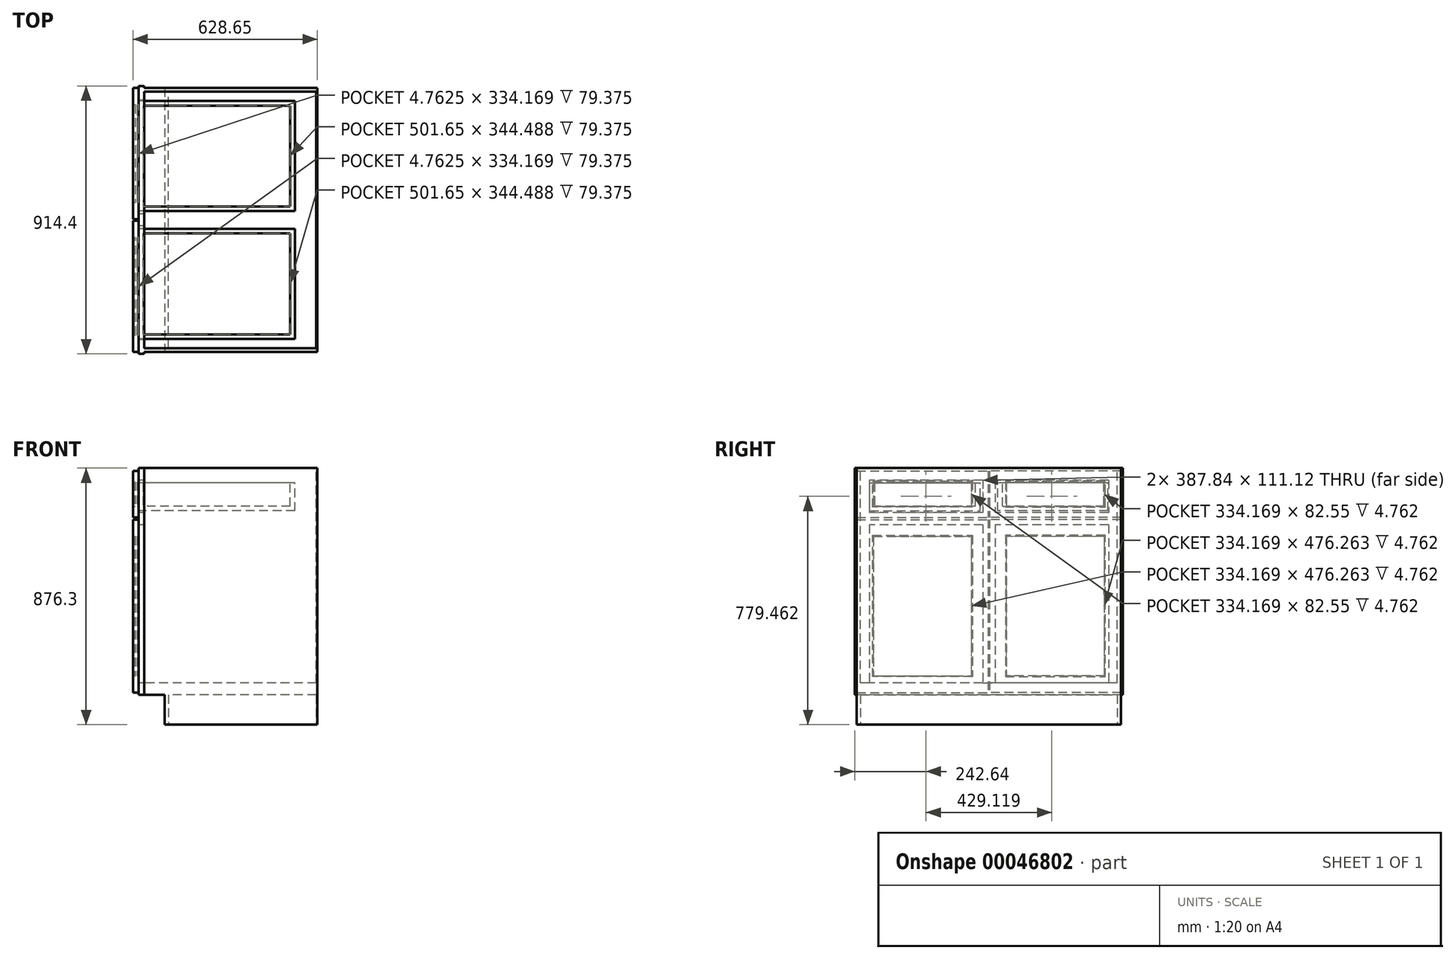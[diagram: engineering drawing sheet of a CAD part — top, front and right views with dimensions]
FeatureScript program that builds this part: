
annotation { "Feature Type Name" : "Feature", "Feature Type Description" : "" }
export const myFeature = defineFeature(function(context is Context, id is Id, definition is map)
    precondition{}
    {
        {
            var Q0;
            Q0=qCreatedBy(makeId("Front.planeOp"),FACE);
            var sketch = newSketch(context, id + "F0", { "sketchPlane" : qUnion([Q0])});
            skLineSegment(sketch, "E0.bottom", {"start": v(-304.8, -438.15) * mm, "end": v(304.8, -438.15) * mm});
            skLineSegment(sketch, "E0.top", {"start": v(-304.8, 438.15) * mm, "end": v(304.8, 438.15) * mm});
            skLineSegment(sketch, "E0.left", {"start": v(-304.8, -438.15) * mm, "end": v(-304.8, 438.15) * mm});
            skLineSegment(sketch, "E0.right", {"start": v(304.8, -438.15) * mm, "end": v(304.8, 438.15) * mm});
            skLineSegment(sketch, "E1", {"start": v(-304.8, -438.15) * mm, "end": v(304.8, 438.15) * mm, "construction": true});
            skSolve(sketch);
        }
        {
            var Q0;
            Q0=qSketchRegion(id+"F0",true);
            extrude(context, id + "F1", {"entities" : qUnion([Q0]), "oppositeDirection" : true, "depth" : 914.4 * mm});
        }
        {
            var Q0;
            Q0=makeQuery(id+"F1.opExtrude","CAP_FACE",FACE,{"disambiguationData":[OSD([sQuery(id+"F0.wireOp",EDGE,"E0.bottom"),sQuery(id+"F0.wireOp",EDGE,"E0.top"),sQuery(id+"F0.wireOp",EDGE,"E0.left"),sQuery(id+"F0.wireOp",EDGE,"E0.right")])],"isStart":true});
            var sketch = newSketch(context, id + "F2", { "sketchPlane" : qUnion([Q0])});
            skLineSegment(sketch, "E2.bottom", {"start": v(-304.8, -438.15) * mm, "end": v(-215.9, -438.15) * mm});
            skLineSegment(sketch, "E2.top", {"start": v(-304.8, -336.55) * mm, "end": v(-215.9, -336.55) * mm});
            skLineSegment(sketch, "E2.left", {"start": v(-304.8, -438.15) * mm, "end": v(-304.8, -336.55) * mm});
            skLineSegment(sketch, "E2.right", {"start": v(-215.9, -438.15) * mm, "end": v(-215.9, -336.55) * mm});
            skSolve(sketch);
        }
        {
            var Q0;
            Q0=qSketchRegion(id+"F2",true);
            extrude(context, id + "F3", {"entities" : qUnion([Q0]), "operationType" : NewBodyOperationType.REMOVE, "endBound" : BoundingType.THROUGH_ALL, "oppositeDirection" : true, "depth" : 25.4 * mm});
        }
        {
            var Q0;
            Q0=makeQuery(id+"F1.opExtrude","SWEPT_FACE",FACE,{"disambiguationData":[OSD([sQuery(id+"F0.wireOp",EDGE,"E0.left")])]});
            var sketch = newSketch(context, id + "F4", { "sketchPlane" : qUnion([Q0])});
            skLineSegment(sketch, "E3.bottom", {"start": v(-865.68, 396.88) * mm, "end": v(-48.72, 396.88) * mm});
            skLineSegment(sketch, "E3.top", {"start": v(-865.68, -295.28) * mm, "end": v(-48.72, -295.28) * mm});
            skLineSegment(sketch, "E3.left", {"start": v(-865.68, 396.88) * mm, "end": v(-865.68, -295.28) * mm});
            skLineSegment(sketch, "E3.right", {"start": v(-48.72, 396.88) * mm, "end": v(-48.72, -295.28) * mm});
            skLineSegment(sketch, "E4", {"start": v(-914.4, 438.15) * mm, "end": v(0, -336.55) * mm, "construction": true});
            skSolve(sketch);
        }
        {
            var Q0;
            Q0=qSketchRegion(id+"F4",true);
            extrude(context, id + "F5", {"entities" : qUnion([Q0]), "operationType" : NewBodyOperationType.REMOVE, "oppositeDirection" : true, "depth" : 19.05 * mm});
        }
        {
            var Q0;
            Q0=makeQuery(id+"F1.opExtrude","SWEPT_FACE",FACE,{"disambiguationData":[OSD([sQuery(id+"F0.wireOp",EDGE,"E0.top")])]});
            var sketch = newSketch(context, id + "F6", { "sketchPlane" : qUnion([Q0])});
            skLineSegment(sketch, "E5.bottom", {"start": v(304.8, 914.4) * mm, "end": v(-285.75, 914.4) * mm});
            skLineSegment(sketch, "E5.top", {"start": v(304.8, 908.05) * mm, "end": v(-285.75, 908.05) * mm});
            skLineSegment(sketch, "E5.left", {"start": v(304.8, 914.4) * mm, "end": v(304.8, 908.05) * mm});
            skLineSegment(sketch, "E5.right", {"start": v(-285.75, 914.4) * mm, "end": v(-285.75, 908.05) * mm});
            skLineSegment(sketch, "E6.bottom", {"start": v(304.8, 0) * mm, "end": v(-285.75, 0) * mm});
            skLineSegment(sketch, "E6.top", {"start": v(304.8, 6.35) * mm, "end": v(-285.75, 6.35) * mm});
            skLineSegment(sketch, "E6.left", {"start": v(304.8, 0) * mm, "end": v(304.8, 6.35) * mm});
            skLineSegment(sketch, "E6.right", {"start": v(-285.75, 0) * mm, "end": v(-285.75, 6.35) * mm});
            skSolve(sketch);
        }
        {
            var Q0;
            Q0=qSketchRegion(id+"F6",true);
            extrude(context, id + "F7", {"entities" : qUnion([Q0]), "operationType" : NewBodyOperationType.REMOVE, "endBound" : BoundingType.THROUGH_ALL, "oppositeDirection" : true, "depth" : 25.4 * mm});
        }
        {
            var Q0;
            Q0=makeQuery(id+"F1.opExtrude","SWEPT_FACE",FACE,{"disambiguationData":[OSD([sQuery(id+"F0.wireOp",EDGE,"E0.top")])]});
            var sketch = newSketch(context, id + "F8", { "sketchPlane" : qUnion([Q0])});
            skLineSegment(sketch, "E7.bottom", {"start": v(301.62, 895.35) * mm, "end": v(-285.75, 895.35) * mm});
            skLineSegment(sketch, "E7.top", {"start": v(301.63, 19.05) * mm, "end": v(-285.75, 19.05) * mm});
            skLineSegment(sketch, "E7.left", {"start": v(301.62, 895.35) * mm, "end": v(301.63, 19.05) * mm});
            skLineSegment(sketch, "E7.right", {"start": v(-285.75, 895.35) * mm, "end": v(-285.75, 19.05) * mm});
            skSolve(sketch);
        }
        {
            var Q0;
            Q0=qSketchRegion(id+"F8",true);
            var Q1;
            Q1=makeQuery(id+"F5.boolean.opBoolean","COPY",FACE,{"derivedFrom":makeQuery(id+"F5.opExtrude","SWEPT_FACE",FACE,{"disambiguationData":[OSD([sQuery(id+"F4.wireOp",EDGE,"E3.top")])]})});
            extrude(context, id + "F9", {"entities" : qUnion([Q0]), "operationType" : NewBodyOperationType.REMOVE, "endBound" : BoundingType.UP_TO_SURFACE, "oppositeDirection" : true, "endBoundEntityFace" : qUnion([Q1]), "depth" : 25.4 * mm});
        }
        {
            var Q0;
            Q0=makeQuery(id+"F1.opExtrude","SWEPT_FACE",FACE,{"disambiguationData":[OSD([sQuery(id+"F0.wireOp",EDGE,"E0.left")])]});
            var sketch = newSketch(context, id + "F10", { "sketchPlane" : qUnion([Q0])});
            skLineSegment(sketch, "E8.bottom", {"start": v(-865.68, 285.75) * mm, "end": v(-48.72, 285.75) * mm});
            skLineSegment(sketch, "E8.top", {"start": v(-865.68, 244.47) * mm, "end": v(-48.72, 244.47) * mm});
            skLineSegment(sketch, "E8.left", {"start": v(-865.68, 285.75) * mm, "end": v(-865.68, 244.47) * mm});
            skLineSegment(sketch, "E8.right", {"start": v(-48.72, 285.75) * mm, "end": v(-48.72, 244.47) * mm});
            skLineSegment(sketch, "E9", {"start": v(-457.2, 396.88) * mm, "end": v(-457.2, -295.28) * mm, "construction": true});
            skLineSegment(sketch, "E10.bottom", {"start": v(-477.84, 396.88) * mm, "end": v(-436.56, 396.88) * mm});
            skLineSegment(sketch, "E10.top", {"start": v(-477.84, -295.28) * mm, "end": v(-436.56, -295.28) * mm});
            skLineSegment(sketch, "E10.left", {"start": v(-477.84, 396.87) * mm, "end": v(-477.84, -295.28) * mm});
            skLineSegment(sketch, "E10.right", {"start": v(-436.56, 396.87) * mm, "end": v(-436.56, -295.28) * mm});
            skSolve(sketch);
        }
        {
            var Q0;
            Q0=qSketchRegion(id+"F10",true);
            var Q1;
            Q1=makeQuery(id+"F9.boolean.opBoolean","COPY",FACE,{"derivedFrom":makeQuery(id+"F9.opExtrude","SWEPT_FACE",FACE,{"disambiguationData":[OSD([sQuery(id+"F8.wireOp",EDGE,"E7.right")])]})});
            extrude(context, id + "F11", {"entities" : qUnion([Q0]), "operationType" : NewBodyOperationType.ADD, "endBound" : BoundingType.UP_TO_SURFACE, "oppositeDirection" : true, "endBoundEntityFace" : qUnion([Q1]), "depth" : 25.4 * mm});
        }
        {
            var Q0;
            Q0=makeQuery(id+"F11.boolean.opBoolean","MERGE",FACE,{"derivedFrom":[makeQuery(id+"F1.opExtrude","SWEPT_FACE",FACE,{"disambiguationData":[OSD([sQuery(id+"F0.wireOp",EDGE,"E0.left")])]}),makeQuery(id+"F11.opExtrude","CAP_FACE",FACE,{"disambiguationData":[OSD([sQuery(id+"F10.wireOp",EDGE,"E8.bottom"),sQuery(id+"F10.wireOp",EDGE,"E8.top"),sQuery(id+"F10.wireOp",EDGE,"E8.left"),sQuery(id+"F10.wireOp",EDGE,"E8.right")])],"isStart":true})]});
            var sketch = newSketch(context, id + "F12", { "sketchPlane" : qUnion([Q0])});
            skLineSegment(sketch, "E11.bottom", {"start": v(-908.05, 261.95) * mm, "end": v(-459.58, 261.95) * mm});
            skLineSegment(sketch, "E11.top", {"start": v(-908.05, -328.61) * mm, "end": v(-459.58, -328.61) * mm});
            skLineSegment(sketch, "E11.left", {"start": v(-908.05, 261.95) * mm, "end": v(-908.05, -328.61) * mm});
            skLineSegment(sketch, "E11.right", {"start": v(-459.58, 261.95) * mm, "end": v(-459.58, -328.61) * mm});
            skLineSegment(sketch, "E12.bottom", {"start": v(-850.9, 204.8) * mm, "end": v(-516.73, 204.8) * mm});
            skLineSegment(sketch, "E12.top", {"start": v(-850.9, -271.46) * mm, "end": v(-516.73, -271.46) * mm});
            skLineSegment(sketch, "E12.left", {"start": v(-850.9, 204.8) * mm, "end": v(-850.9, -271.46) * mm});
            skLineSegment(sketch, "E12.right", {"start": v(-516.73, 204.8) * mm, "end": v(-516.73, -271.46) * mm});
            skSolve(sketch);
        }
        {
            var Q0;
            Q0=qSketchRegion(id+"F12",true);
            extrude(context, id + "F13", {"entities" : qUnion([Q0]), "depth" : 19.05 * mm});
        }
        {
            var Q0;
            Q0=makeQuery(id+"F13.opExtrude","SWEPT_FACE",FACE,{"disambiguationData":[OSD([sQuery(id+"F12.wireOp",EDGE,"E12.top")])]});
            var sketch = newSketch(context, id + "F14", { "sketchPlane" : qUnion([Q0])});
            skLineSegment(sketch, "E13.bottom", {"start": v(-315.91, 850.9) * mm, "end": v(-309.56, 850.9) * mm});
            skLineSegment(sketch, "E13.top", {"start": v(-315.91, 516.73) * mm, "end": v(-309.56, 516.73) * mm});
            skLineSegment(sketch, "E13.left", {"start": v(-315.91, 850.9) * mm, "end": v(-315.91, 516.73) * mm});
            skLineSegment(sketch, "E13.right", {"start": v(-309.56, 850.9) * mm, "end": v(-309.56, 516.73) * mm});
            skSolve(sketch);
        }
        {
            var Q0;
            Q0=qSketchRegion(id+"F14",true);
            extrude(context, id + "F15", {"entities" : qUnion([Q0]), "operationType" : NewBodyOperationType.ADD, "endBound" : BoundingType.UP_TO_NEXT, "depth" : 25.4 * mm});
        }
        {
            var Q0;
            Q0=makeQuery(id+"F13.opExtrude","CAP_EDGE",EDGE,{"disambiguationData":[OSD([sQuery(id+"F12.wireOp",EDGE,"E12.left")])],"isStart":false});
            var Q1;
            Q1=makeQuery(id+"F13.opExtrude","CAP_EDGE",EDGE,{"disambiguationData":[OSD([sQuery(id+"F12.wireOp",EDGE,"E12.top")])],"isStart":false});
            var Q2;
            Q2=makeQuery(id+"F13.opExtrude","CAP_EDGE",EDGE,{"disambiguationData":[OSD([sQuery(id+"F12.wireOp",EDGE,"E12.right")])],"isStart":false});
            var Q3;
            Q3=makeQuery(id+"F13.opExtrude","CAP_EDGE",EDGE,{"disambiguationData":[OSD([sQuery(id+"F12.wireOp",EDGE,"E12.bottom")])],"isStart":false});
            chamfer(context, id + "F16", {"entities" : qUnion([Q0, Q1, Q2, Q3]), "width" : 3.17 * mm, "tangentPropagation" : true});
        }
        {
            var Q0;
            Q0=makeQuery(id+"F11.boolean.opBoolean","MERGE",FACE,{"derivedFrom":[makeQuery(id+"F1.opExtrude","SWEPT_FACE",FACE,{"disambiguationData":[OSD([sQuery(id+"F0.wireOp",EDGE,"E0.left")])]}),makeQuery(id+"F11.opExtrude","CAP_FACE",FACE,{"disambiguationData":[OSD([sQuery(id+"F10.wireOp",EDGE,"E8.bottom"),sQuery(id+"F10.wireOp",EDGE,"E8.top"),sQuery(id+"F10.wireOp",EDGE,"E8.left"),sQuery(id+"F10.wireOp",EDGE,"E8.right")])],"isStart":true})]});
            var sketch = newSketch(context, id + "F17", { "sketchPlane" : qUnion([Q0])});
            skLineSegment(sketch, "E14.bottom", {"start": v(-908.05, 428.62) * mm, "end": v(-459.58, 428.62) * mm});
            skLineSegment(sketch, "E14.top", {"start": v(-908.05, 269.88) * mm, "end": v(-459.58, 269.88) * mm});
            skLineSegment(sketch, "E14.left", {"start": v(-908.05, 428.62) * mm, "end": v(-908.05, 269.88) * mm});
            skLineSegment(sketch, "E14.right", {"start": v(-459.58, 428.62) * mm, "end": v(-459.58, 269.88) * mm});
            skLineSegment(sketch, "E15.bottom", {"start": v(-850.9, 390.52) * mm, "end": v(-516.73, 390.52) * mm});
            skLineSegment(sketch, "E15.top", {"start": v(-850.9, 307.98) * mm, "end": v(-516.73, 307.98) * mm});
            skLineSegment(sketch, "E15.left", {"start": v(-850.9, 390.52) * mm, "end": v(-850.9, 307.98) * mm});
            skLineSegment(sketch, "E15.right", {"start": v(-516.73, 390.52) * mm, "end": v(-516.73, 307.98) * mm});
            skSolve(sketch);
        }
        {
            var Q0;
            Q0=qSketchRegion(id+"F17",true);
            extrude(context, id + "F18", {"entities" : qUnion([Q0]), "depth" : 19.05 * mm});
        }
        {
            var Q0;
            Q0=makeQuery(id+"F18.opExtrude","SWEPT_FACE",FACE,{"disambiguationData":[OSD([sQuery(id+"F17.wireOp",EDGE,"E15.top")])]});
            var sketch = newSketch(context, id + "F19", { "sketchPlane" : qUnion([Q0])});
            skLineSegment(sketch, "E16.bottom", {"start": v(-309.56, 850.9) * mm, "end": v(-315.91, 850.9) * mm});
            skLineSegment(sketch, "E16.top", {"start": v(-309.56, 516.73) * mm, "end": v(-315.91, 516.73) * mm});
            skLineSegment(sketch, "E16.left", {"start": v(-309.56, 850.9) * mm, "end": v(-309.56, 516.73) * mm});
            skLineSegment(sketch, "E16.right", {"start": v(-315.91, 850.9) * mm, "end": v(-315.91, 516.73) * mm});
            skSolve(sketch);
        }
        {
            var Q0;
            Q0=qSketchRegion(id+"F19",true);
            var Q1;
            Q1=makeQuery(id+"F18.opExtrude","SWEPT_FACE",FACE,{"disambiguationData":[OSD([sQuery(id+"F17.wireOp",EDGE,"E15.bottom")])]});
            extrude(context, id + "F20", {"entities" : qUnion([Q0]), "operationType" : NewBodyOperationType.ADD, "endBound" : BoundingType.UP_TO_SURFACE, "endBoundEntityFace" : qUnion([Q1]), "depth" : 25.4 * mm});
        }
        {
            var Q0;
            Q0=makeQuery(id+"F18.opExtrude","CAP_EDGE",EDGE,{"disambiguationData":[OSD([sQuery(id+"F17.wireOp",EDGE,"E15.top")])],"isStart":false});
            var Q1;
            Q1=makeQuery(id+"F18.opExtrude","CAP_EDGE",EDGE,{"disambiguationData":[OSD([sQuery(id+"F17.wireOp",EDGE,"E15.left")])],"isStart":false});
            var Q2;
            Q2=makeQuery(id+"F18.opExtrude","CAP_EDGE",EDGE,{"disambiguationData":[OSD([sQuery(id+"F17.wireOp",EDGE,"E15.bottom")])],"isStart":false});
            var Q3;
            Q3=makeQuery(id+"F18.opExtrude","CAP_EDGE",EDGE,{"disambiguationData":[OSD([sQuery(id+"F17.wireOp",EDGE,"E15.right")])],"isStart":false});
            chamfer(context, id + "F21", {"entities" : qUnion([Q0, Q1, Q2, Q3]), "width" : 3.17 * mm, "tangentPropagation" : true});
        }
        {
            var Q0;
            Q0=makeQuery(id+"F1.opExtrude","SWEPT_FACE",FACE,{"disambiguationData":[OSD([sQuery(id+"F0.wireOp",EDGE,"E0.bottom")])]});
            var sketch = newSketch(context, id + "F22", { "sketchPlane" : qUnion([Q0])});
            skLineSegment(sketch, "E17.bottom", {"start": v(301.63, -19.05) * mm, "end": v(-203.2, -19.05) * mm});
            skLineSegment(sketch, "E17.top", {"start": v(301.63, -895.35) * mm, "end": v(-203.2, -895.35) * mm});
            skLineSegment(sketch, "E17.left", {"start": v(301.63, -19.05) * mm, "end": v(301.63, -895.35) * mm});
            skLineSegment(sketch, "E17.right", {"start": v(-203.2, -19.05) * mm, "end": v(-203.2, -895.35) * mm});
            skSolve(sketch);
        }
        {
            var Q0;
            Q0=qSketchRegion(id+"F22",true);
            extrude(context, id + "F23", {"entities" : qUnion([Q0]), "operationType" : NewBodyOperationType.REMOVE, "oppositeDirection" : true, "depth" : 101.6 * mm});
        }
        {
            var Q0;
            Q0=makeQuery(id+"F18.opExtrude","CAP_FACE",FACE,{"disambiguationData":[OSD([sQuery(id+"F17.wireOp",EDGE,"E14.bottom"),sQuery(id+"F17.wireOp",EDGE,"E14.top"),sQuery(id+"F17.wireOp",EDGE,"E14.left"),sQuery(id+"F17.wireOp",EDGE,"E14.right"),sQuery(id+"F17.wireOp",EDGE,"E15.bottom"),sQuery(id+"F17.wireOp",EDGE,"E15.top"),sQuery(id+"F17.wireOp",EDGE,"E15.left"),sQuery(id+"F17.wireOp",EDGE,"E15.right")])],"isStart":true});
            var sketch = newSketch(context, id + "F24", { "sketchPlane" : qUnion([Q0])});
            skLineSegment(sketch, "E18.bottom", {"start": v(863.6, 292.1) * mm, "end": v(487.36, 292.1) * mm});
            skLineSegment(sketch, "E18.top", {"start": v(863.6, 387.35) * mm, "end": v(487.36, 387.35) * mm});
            skLineSegment(sketch, "E18.left", {"start": v(863.6, 292.1) * mm, "end": v(863.6, 387.35) * mm});
            skLineSegment(sketch, "E18.right", {"start": v(487.36, 292.1) * mm, "end": v(487.36, 387.35) * mm});
            skSolve(sketch);
        }
        {
            var Q0;
            Q0=qSketchRegion(id+"F24",true);
            extrude(context, id + "F25", {"entities" : qUnion([Q0]), "operationType" : NewBodyOperationType.ADD, "depth" : 533.4 * mm});
        }
        {
            var Q0;
            Q0=makeQuery(id+"F25.opExtrude","SWEPT_FACE",FACE,{"disambiguationData":[OSD([sQuery(id+"F24.wireOp",EDGE,"E18.top")])]});
            shell(context, id + "F26", {"entities" : qUnion([Q0]), "thickness" : 15.88 * mm});
        }
        {
            var Q0;
            Q0=sQuery(id+"F10.wireOp",EDGE,"E10.bottom");
            var Q1;
            Q1=sQuery(id+"F10.wireOp",VERTEX,"E9.start");
            cPlane(context, id + "F27", {"entities" : qUnion([Q0, Q1]), "cplaneType" : CPlaneType.LINE_POINT, "offset" : 152.4 * mm, "width" : 152.4 * mm, "height" : 152.4 * mm});
        }
        {
            var Q0;
            Q0=makeQuery(id+"F18.opExtrude","SWEPT_BODY",BODY,{"disambiguationData":[OSD([sQuery(id+"F17.wireOp",EDGE,"E14.bottom"),sQuery(id+"F17.wireOp",EDGE,"E14.top"),sQuery(id+"F17.wireOp",EDGE,"E14.left"),sQuery(id+"F17.wireOp",EDGE,"E14.right"),sQuery(id+"F17.wireOp",EDGE,"E15.bottom"),sQuery(id+"F17.wireOp",EDGE,"E15.top"),sQuery(id+"F17.wireOp",EDGE,"E15.left"),sQuery(id+"F17.wireOp",EDGE,"E15.right")])]});
            var Q1;
            Q1=qCreatedBy(id+"F27.planeOp",FACE);
            mirror(context, id + "F28", {"entities" : qUnion([Q0]), "mirrorPlane" : qUnion([Q1])});
        }
        {
            var Q0;
            Q0=makeQuery(id+"F13.opExtrude","SWEPT_BODY",BODY,{"disambiguationData":[OSD([sQuery(id+"F12.wireOp",EDGE,"E11.bottom"),sQuery(id+"F12.wireOp",EDGE,"E11.top"),sQuery(id+"F12.wireOp",EDGE,"E11.left"),sQuery(id+"F12.wireOp",EDGE,"E11.right"),sQuery(id+"F12.wireOp",EDGE,"E12.bottom"),sQuery(id+"F12.wireOp",EDGE,"E12.top"),sQuery(id+"F12.wireOp",EDGE,"E12.left"),sQuery(id+"F12.wireOp",EDGE,"E12.right")])]});
            var Q1;
            Q1=qCreatedBy(id+"F27.planeOp",FACE);
            mirror(context, id + "F29", {"entities" : qUnion([Q0]), "mirrorPlane" : qUnion([Q1])});
        }
    });
